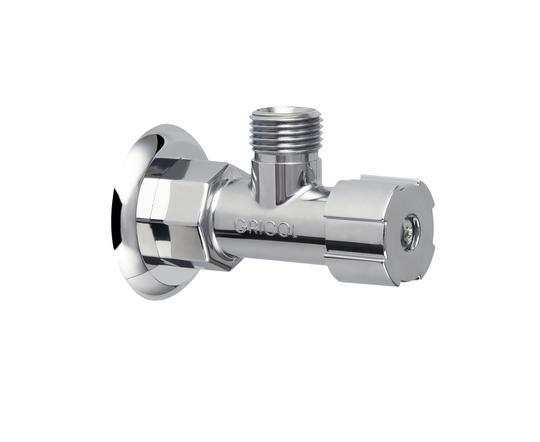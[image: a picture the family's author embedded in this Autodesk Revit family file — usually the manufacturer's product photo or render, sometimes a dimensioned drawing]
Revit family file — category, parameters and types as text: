
# Revit family: BIM_01-3201-11
name_source: partatom
category: Plumbing Fixtures
units: mm (PartAtom-declared; Revit-internal decimal feet)

## family parameters
Classification Number = 23.31.11.00
Cut with Voids When Loaded = No
Enable Cutting in Views = No
Host = Face
Maintain Annotation Orientation = No
Part Type = Normal
Room Calculation Point = No
Round Connector Dimension = Use Diameter
Shared = No

## types (1)
- 01-3201-11
    Ancho = 83.5 mm  [stored 0.27395 ft]
    CW Connection = Yes
    Conexiones = Acometida: Rosca Hembra 1/2” NPT. Salida:
Rosca Macho 1/2” NPSM.
    Date Modified = 22/08/2025
    Default Elevation = 0 mm  [stored 0 ft]
    Description = Llave
    Diametro escudo = 50.6 mm
    Diametro nominal = 15.9 Nm
    Garantia Especifica = 20 AÑOS
    HW Connection = Yes
    Link Ficha Tecnica = https://infotecnica.gricol.com
    Manufacturer = Gricol
    Materiales del producto = ABS, Latón, Caucho
    Model = 01-3201-11
    Plastico - ABS Cromado = Plastico - ABS Cromado
    Presión Maxima = 125.00 psi
    Presión Mínima = 20.00 psi
    Presión de Estallído = 500.00 psi
    Product Name = Llave De Regulación Plástica Cromada
    Referente Normativo = NTC 1644, ASME A112.18.1 / CSA B125.1
    Resistencia a Corrosión = NTC 1156 Sal Neutral
    Rosca NPSM 1/2" = 1/2"
    Rosca NPT 1/2" = 1/2"
    Sitio web = https://www.gricol.com
    Temperaturas de trabajo = DE 5° A 71°
    Tipo de Uso = Domestico
    Torque de Conexión = 61 Nm
    Torque de operación = 1,7 Nm
    Type Image = LLAVE DE REGULACION PLASTICA CROMADA.jpg
    URL = https://www.gricol.com
    Vent Connection = No
    Vida Util = 2000 CICLOS
    Waste Connection = No

note: [stored X ft] marks values corroborated as IEEE doubles in the binary element streams (Revit-internal decimal feet)

## geometry (parser evidence)
native form markers: Blend x4, Sweep x4
no freeform markers — native parametric forms only
